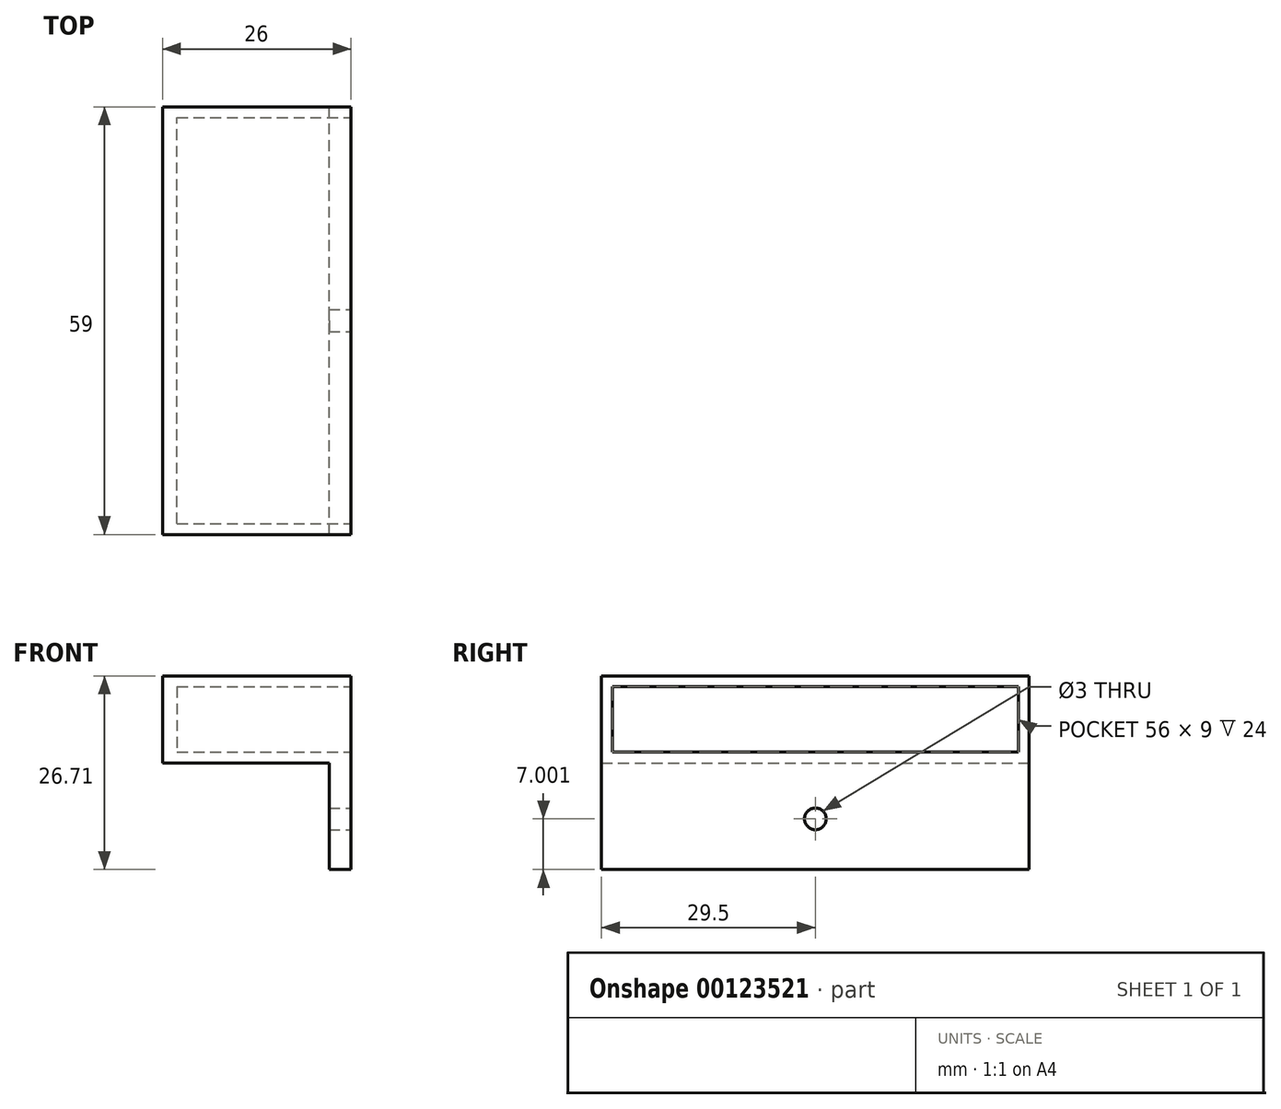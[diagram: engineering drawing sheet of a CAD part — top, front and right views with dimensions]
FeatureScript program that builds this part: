
annotation { "Feature Type Name" : "Feature", "Feature Type Description" : "" }
export const myFeature = defineFeature(function(context is Context, id is Id, definition is map)
    precondition{}
    {
        {
            var Q0;
            Q0=qCreatedBy(makeId("Front.planeOp"),FACE);
            var sketch = newSketch(context, id + "F0", { "sketchPlane" : qUnion([Q0])});
            skLineSegment(sketch, "E0.bottom", {"start": v(-38, 12) * mm, "end": v(-12, 12) * mm});
            skLineSegment(sketch, "E0.top", {"start": v(-38, 0) * mm, "end": v(-12, 0) * mm});
            skLineSegment(sketch, "E0.left", {"start": v(-38, 12) * mm, "end": v(-38, 0) * mm});
            skLineSegment(sketch, "E0.right", {"start": v(-12, 12) * mm, "end": v(-12, 0) * mm});
            skLineSegment(sketch, "E1", {"start": v(0, 0) * mm, "end": v(0, 0) * mm});
            skLineSegment(sketch, "E2", {"start": v(-12, 0) * mm, "end": v(-12, -14.7) * mm});
            skLineSegment(sketch, "E3", {"start": v(-12, -14.7) * mm, "end": v(-15, -14.7) * mm});
            skLineSegment(sketch, "E4", {"start": v(-15, -14.7) * mm, "end": v(-15, 0) * mm});
            skSolve(sketch);
        }
        {
            var Q0;
            Q0 = qSketchRegion(id + "F0", true);
            extrude(context, id + "F1", {"entities" : qUnion([Q0]), "depth" : 59 * mm});
        }
        {
            var Q0;
            Q0=makeQuery(id+"F1.opExtrude","SWEPT_FACE",FACE,{"disambiguationData":[OSD([sQuery(id+"F0.wireOp",EDGE,"E0.right"),sQuery(id+"F0.wireOp",EDGE,"E2")])]});
            var sketch = newSketch(context, id + "F2", { "sketchPlane" : qUnion([Q0])});
            skLineSegment(sketch, "E5.bottom", {"start": v(-57.5, 10.5) * mm, "end": v(-1.5, 10.5) * mm});
            skLineSegment(sketch, "E5.top", {"start": v(-57.5, 1.5) * mm, "end": v(-1.5, 1.5) * mm});
            skLineSegment(sketch, "E5.left", {"start": v(-57.5, 10.5) * mm, "end": v(-57.5, 1.5) * mm});
            skLineSegment(sketch, "E5.right", {"start": v(-1.5, 10.5) * mm, "end": v(-1.5, 1.5) * mm});
            skCircle(sketch, "E6", {"center": v(-29.5, -7.7) * mm, "radius": 1.5 * mm});
            skSolve(sketch);
        }
        {
            var Q0;
            Q0=makeQuery(id+"F2.imprint","IMPRINT",FACE,{"disambiguationData":[TD([[makeQuery(id+"F2.imprint","IMPRINT",EDGE,{"derivedFrom":sQuery(id+"F2.wireOp",EDGE,"E6")}),1.0]])]});
            extrude(context, id + "F3", {"entities" : qUnion([Q0]), "operationType" : NewBodyOperationType.REMOVE, "oppositeDirection" : true, "depth" : 4 * mm});
        }
        {
            var Q0;
            Q0 = qSketchRegion(id + "F2", true);
            extrude(context, id + "F4", {"entities" : qUnion([Q0]), "operationType" : NewBodyOperationType.REMOVE, "oppositeDirection" : true, "depth" : 24 * mm});
        }
    });
